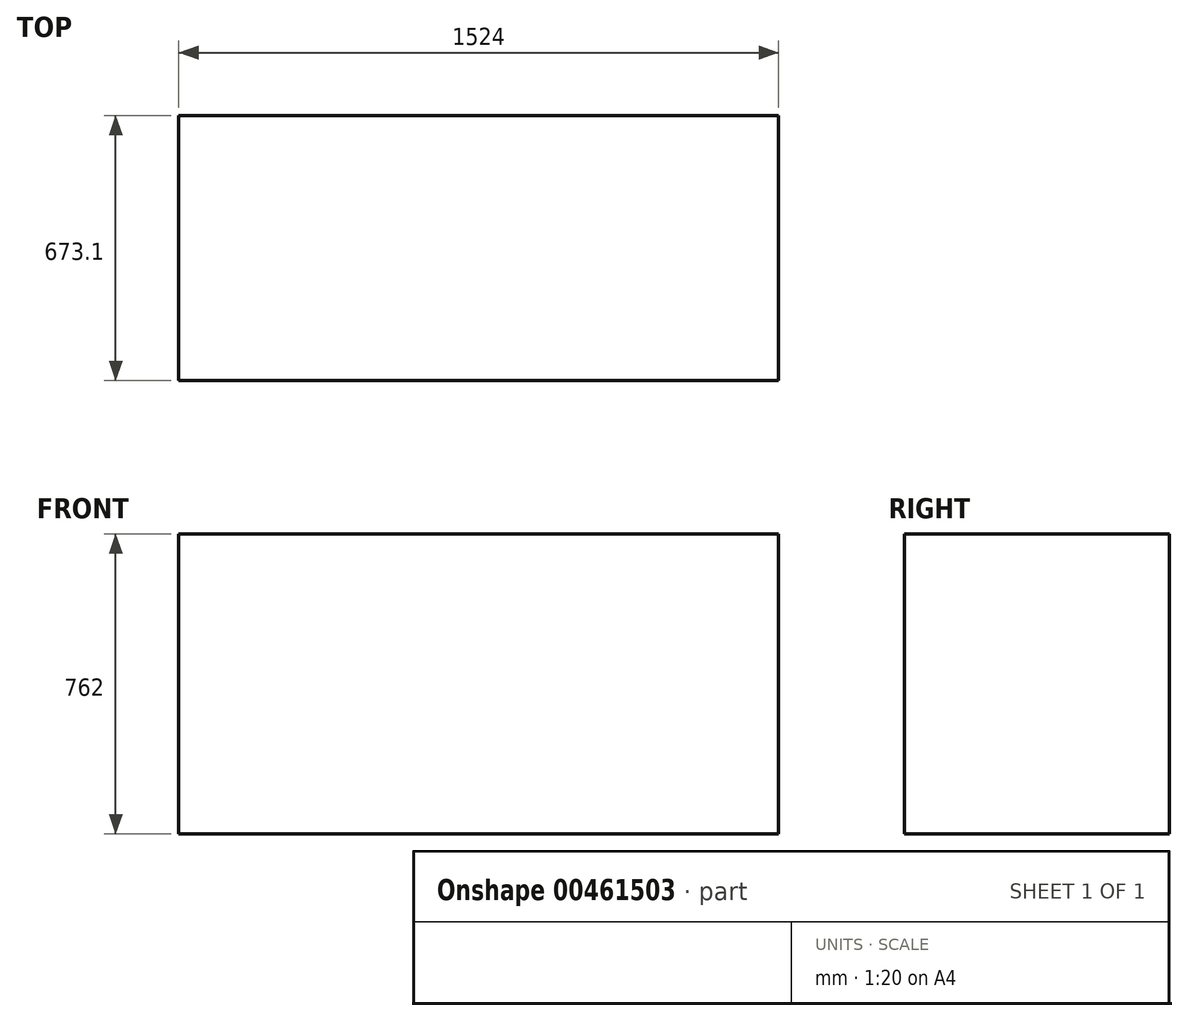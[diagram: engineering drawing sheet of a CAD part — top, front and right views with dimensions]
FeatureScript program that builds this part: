
annotation { "Feature Type Name" : "Feature", "Feature Type Description" : "" }
export const myFeature = defineFeature(function(context is Context, id is Id, definition is map)
    precondition{}
    {
        {
            var Q0;
            Q0=qCreatedBy(makeId("Front.planeOp"),FACE);
            var sketch = newSketch(context, id + "F0", { "sketchPlane" : qUnion([Q0])});
            skLineSegment(sketch, "E0.bottom", {"start": v(-1524, 762) * mm, "end": v(0, 762) * mm});
            skLineSegment(sketch, "E0.top", {"start": v(-1524, 0) * mm, "end": v(0, 0) * mm});
            skLineSegment(sketch, "E0.left", {"start": v(-1524, 762) * mm, "end": v(-1524, 0) * mm});
            skLineSegment(sketch, "E0.right", {"start": v(0, 762) * mm, "end": v(0, 0) * mm});
            skSolve(sketch);
        }
        {
            var Q0;
            Q0=makeQuery(id+"F0.imprint","IMPRINT",FACE,{"disambiguationData":[TD([[makeQuery(id+"F0.imprint","IMPRINT",EDGE,{"derivedFrom":sQuery(id+"F0.wireOp",EDGE,"E0.bottom")}),-1.0]])]});
            extrude(context, id + "F1", {"entities" : qUnion([Q0]), "depth" : 673.1 * mm});
        }
    });
